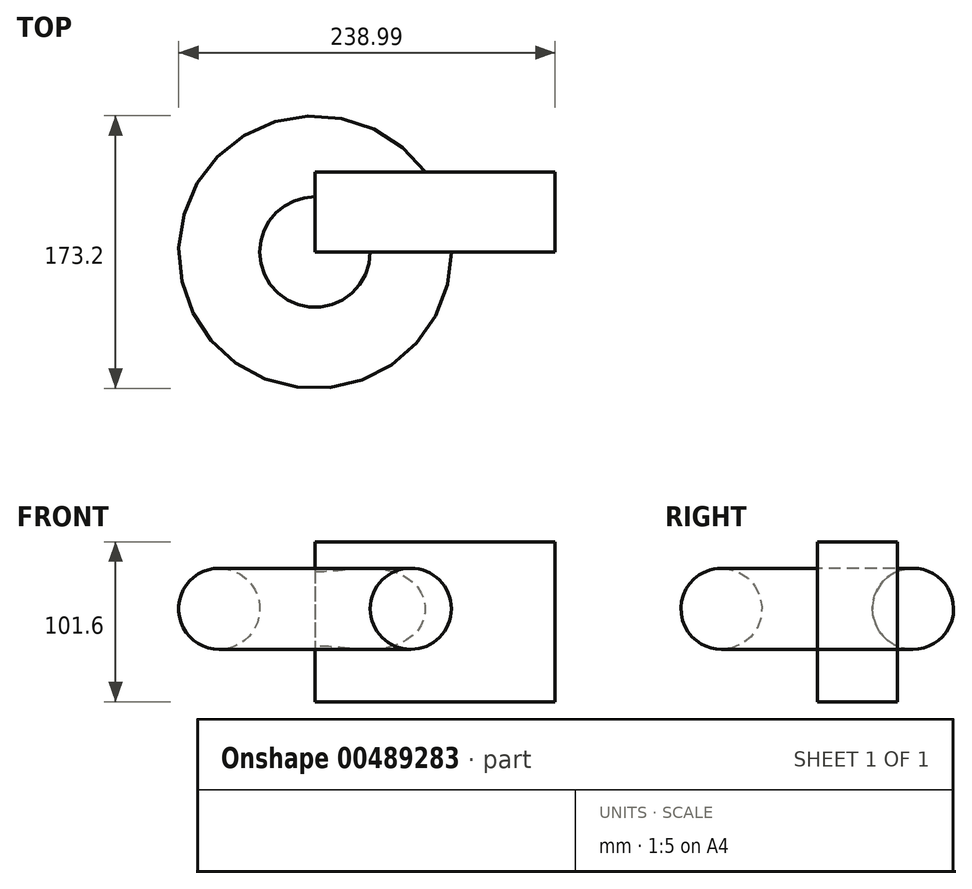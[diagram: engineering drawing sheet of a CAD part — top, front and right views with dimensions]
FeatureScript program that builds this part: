
annotation { "Feature Type Name" : "Feature", "Feature Type Description" : "" }
export const myFeature = defineFeature(function(context is Context, id is Id, definition is map)
    precondition{}
    {
        {
            var Q0;
            Q0=qCreatedBy(makeId("Front.planeOp"),FACE);
            var sketch = newSketch(context, id + "F0", { "sketchPlane" : qUnion([Q0])});
            skLineSegment(sketch, "E0.bottom", {"start": v(-30.43, 101.6) * mm, "end": v(121.97, 101.6) * mm});
            skLineSegment(sketch, "E0.top", {"start": v(-30.43, 0) * mm, "end": v(121.97, 0) * mm});
            skLineSegment(sketch, "E0.left", {"start": v(-30.43, 101.6) * mm, "end": v(-30.43, 0) * mm});
            skLineSegment(sketch, "E0.right", {"start": v(121.97, 101.6) * mm, "end": v(121.97, 0) * mm});
            skSolve(sketch);
        }
        {
            var Q0;
            Q0 = qSketchRegion(id + "F0", true);
            extrude(context, id + "F1", {"entities" : qUnion([Q0]), "endBound" : BoundingType.SYMMETRIC, "depth" : 50.8 * mm});
        }
        {
            var Q0;
            Q0=makeQuery(id+"F1.opExtrude","CAP_FACE",FACE,{"disambiguationData":[OSD([sQuery(id+"F0.wireOp",EDGE,"E0.bottom"),sQuery(id+"F0.wireOp",EDGE,"E0.top"),sQuery(id+"F0.wireOp",EDGE,"E0.left"),sQuery(id+"F0.wireOp",EDGE,"E0.right")])],"isStart":false});
            var sketch = newSketch(context, id + "F2", { "sketchPlane" : qUnion([Q0])});
            skCircle(sketch, "E1", {"center": v(30.42, 59.07) * mm, "radius": 25.75 * mm});
            skSolve(sketch);
        }
        {
            var Q0;
            Q0 = qSketchRegion(id + "F2", true);
            var Q1;
            Q1=makeQuery(id+"F1.opExtrude","CAP_EDGE",EDGE,{"disambiguationData":[OSD([sQuery(id+"F0.wireOp",EDGE,"E0.left")])],"isStart":false});
            revolve(context, id + "F3", {"operationType" : NewBodyOperationType.ADD, "entities" : qUnion([Q0]), "axis" : qUnion([Q1]), "revolveType" : RevolveType.FULL});
        }
    });
